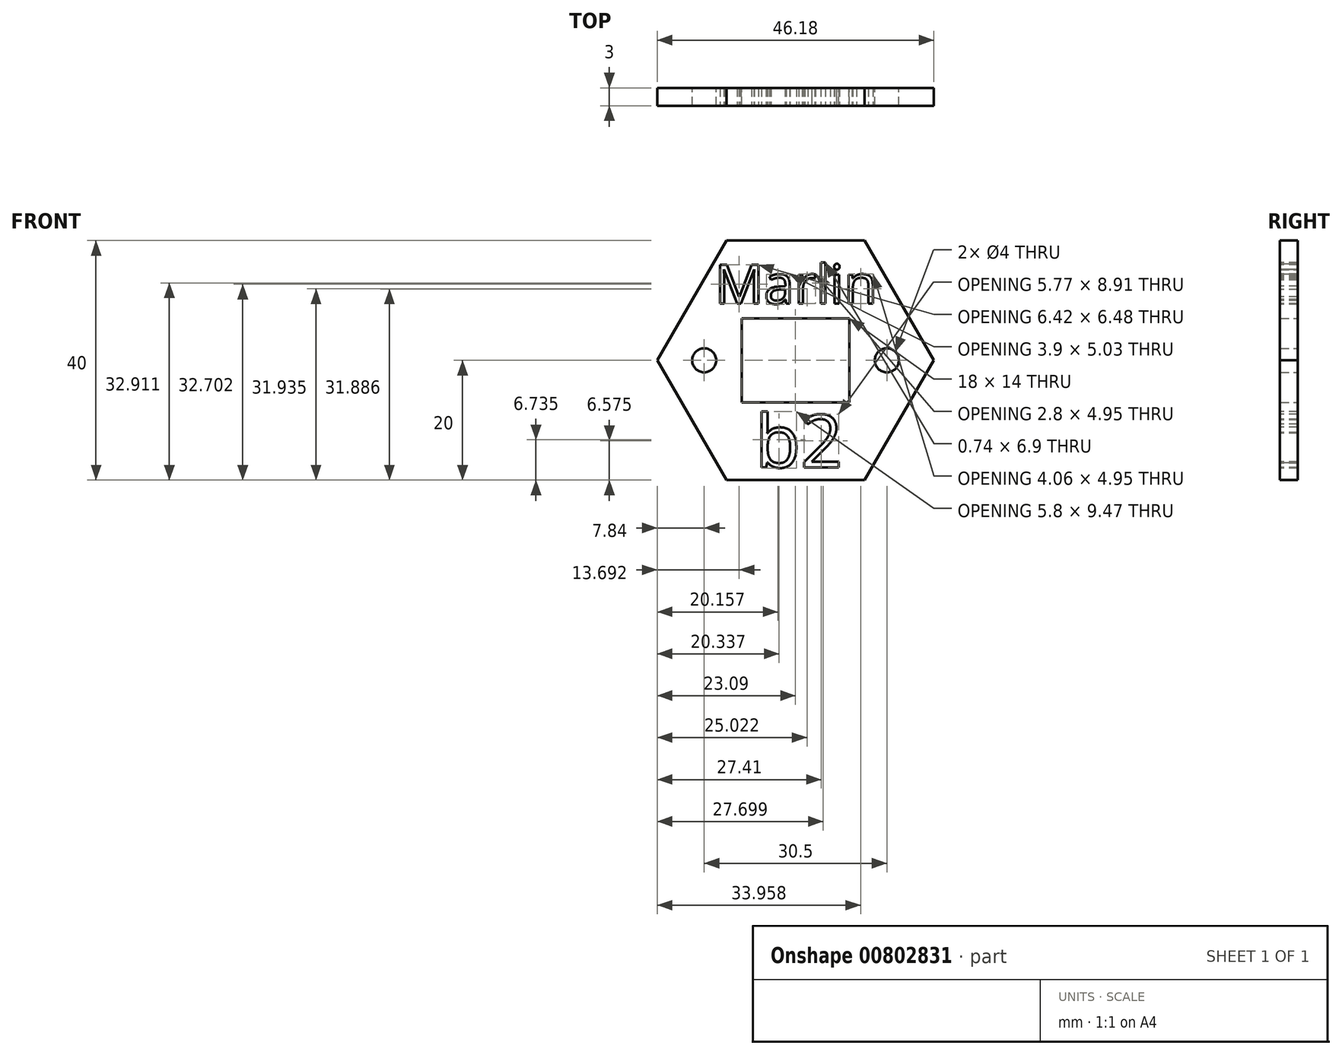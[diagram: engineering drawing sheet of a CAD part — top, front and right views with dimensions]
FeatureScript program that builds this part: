
annotation { "Feature Type Name" : "Feature", "Feature Type Description" : "" }
export const myFeature = defineFeature(function(context is Context, id is Id, definition is map)
    precondition{}
    {
        {
            var Q0;
            Q0=qCreatedBy(makeId("Front.planeOp"),FACE);
            var sketch = newSketch(context, id + "F0", { "sketchPlane" : qUnion([Q0])});
            skCircle(sketch, "E0.cCircle", {"center": v(0, 0) * mm, "radius": 20 * mm, "construction": true});
            skLineSegment(sketch, "E0.0", {"start": v(11.55, -20) * mm, "end": v(-11.55, -20) * mm});
            skLineSegment(sketch, "E0.1", {"start": v(-11.55, -20) * mm, "end": v(-23.1, 0) * mm});
            skLineSegment(sketch, "E0.2", {"start": v(-23.1, 0) * mm, "end": v(-11.55, 20) * mm});
            skLineSegment(sketch, "E0.3", {"start": v(-11.55, 20) * mm, "end": v(11.55, 20) * mm});
            skLineSegment(sketch, "E0.4", {"start": v(11.55, 20) * mm, "end": v(23.1, 0) * mm});
            skLineSegment(sketch, "E0.5", {"start": v(23.1, 0) * mm, "end": v(11.55, -20) * mm});
            skPoint(sketch, "E0.0.midPoint", {"position": v(0, -20) * mm});
            skPoint(sketch, "E1", {"position": v(15.25, 0) * mm});
            skPoint(sketch, "E2", {"position": v(-15.25, 0) * mm});
            skLineSegment(sketch, "E3.bottom", {"start": v(9, -7) * mm, "end": v(-9, -7) * mm});
            skLineSegment(sketch, "E3.top", {"start": v(9, 7) * mm, "end": v(-9, 7) * mm});
            skLineSegment(sketch, "E3.left", {"start": v(9, -7) * mm, "end": v(9, 7) * mm});
            skLineSegment(sketch, "E3.right", {"start": v(-9, -7) * mm, "end": v(-9, 7) * mm});
            skCircle(sketch, "E4", {"center": v(-15.25, 0) * mm, "radius": 2 * mm});
            skCircle(sketch, "E5", {"center": v(15.25, 0) * mm, "radius": 2 * mm});
            skSolve(sketch);
        }
        {
            var Q0;
            Q0=makeQuery(id+"F0.imprint","IMPRINT",FACE,{"disambiguationData":[TD([[makeQuery(id+"F0.imprint","IMPRINT",EDGE,{"derivedFrom":sQuery(id+"F0.wireOp",EDGE,"E0.0")}),-1.0]])]});
            extrude(context, id + "F1", {"entities" : qUnion([Q0]), "depth" : 3 * mm, "offsetDistance" : 25 * mm});
        }
        {
            var Q0;
            Q0=makeQuery(id+"F1.opExtrude","CAP_FACE",FACE,{"disambiguationData":[OSD([sQuery(id+"F0.wireOp",EDGE,"E0.0"),sQuery(id+"F0.wireOp",EDGE,"E0.1"),sQuery(id+"F0.wireOp",EDGE,"E0.2"),sQuery(id+"F0.wireOp",EDGE,"E0.3"),sQuery(id+"F0.wireOp",EDGE,"E0.4"),sQuery(id+"F0.wireOp",EDGE,"E0.5"),sQuery(id+"F0.wireOp",EDGE,"E3.bottom"),sQuery(id+"F0.wireOp",EDGE,"E3.top"),sQuery(id+"F0.wireOp",EDGE,"E3.left"),sQuery(id+"F0.wireOp",EDGE,"E3.right"),sQuery(id+"F0.wireOp",EDGE,"E4"),sQuery(id+"F0.wireOp",EDGE,"E5")])],"isStart":false});
            var sketch = newSketch(context, id + "F2", { "sketchPlane" : qUnion([Q0])});
            skText(sketch, "E6", { "text": "Marlin", "fontName": "OpenSans-Regular.ttf"});
            const initialGuessF2  = {"E6": [-0.0135, 0.00946, 1, 0, 0.00654]};
            skSetInitialGuess(sketch, initialGuessF2);
            skSolve(sketch);
        }
        {
            var Q0;
            Q0 = qSketchRegion(id + "F2", true);
            extrude(context, id + "F3", {"entities" : qUnion([Q0]), "operationType" : NewBodyOperationType.REMOVE, "oppositeDirection" : true, "depth" : 25 * mm, "offsetDistance" : 25 * mm});
        }
        {
            var Q0;
            {var subQ0=sQuery(id+"F0.wireOp",EDGE,"E3.left");var subQ1=sQuery(id+"F0.wireOp",EDGE,"E3.top");var subQ2=sQuery(id+"F0.wireOp",EDGE,"E3.bottom");var subQ3=sQuery(id+"F0.wireOp",EDGE,"E0.5");var subQ4=sQuery(id+"F0.wireOp",EDGE,"E0.4");var subQ5=sQuery(id+"F0.wireOp",EDGE,"E3.right");var subQ6=sQuery(id+"F0.wireOp",EDGE,"E0.0");var subQ7=sQuery(id+"F0.wireOp",EDGE,"E0.3");var subQ8=sQuery(id+"F0.wireOp",EDGE,"E0.1");var subQ9=sQuery(id+"F0.wireOp",EDGE,"E0.2");var subQ10=sQuery(id+"F0.wireOp",EDGE,"E4");var subQ11=sQuery(id+"F0.wireOp",EDGE,"E5");Q0=makeQuery(id+"F3.boolean.opBoolean","SPLIT",FACE,{"disambiguationData":[TD([makeQuery(id+"F1.opExtrude","SWEPT_FACE",FACE,{"disambiguationData":[OSD([subQ6])]})])],"derivedFrom":makeQuery(id+"F1.opExtrude","CAP_FACE",FACE,{"disambiguationData":[OSD([subQ6,subQ8,subQ9,subQ7,subQ4,subQ3,subQ2,subQ1,subQ0,subQ5,subQ10,subQ11])],"isStart":false})});}
            var sketch = newSketch(context, id + "F4", { "sketchPlane" : qUnion([Q0])});
            skText(sketch, "E7", { "text": "b2", "fontName": "OpenSans-Regular.ttf"});
            const initialGuessF4  = {"E7": [-0.00671, -0.01788, 1, 0, 0.00886]};
            skSetInitialGuess(sketch, initialGuessF4);
            skSolve(sketch);
        }
        {
            var Q0;
            Q0=makeQuery(id+"F4.imprint","IMPRINT",FACE,{"disambiguationData":[TD([[makeQuery(id+"F4.imprint","IMPRINT",EDGE,{"derivedFrom":sQuery(id+"F4.wireOp",EDGE,"E7.sketch_text.stroke-0")}),-1.0]])]});
            var Q1;
            Q1=makeQuery(id+"F4.imprint","IMPRINT",FACE,{"disambiguationData":[TD([[makeQuery(id+"F4.imprint","IMPRINT",EDGE,{"derivedFrom":sQuery(id+"F4.wireOp",EDGE,"E7.sketch_text.stroke-23")}),-1.0]])]});
            extrude(context, id + "F5", {"entities" : qUnion([Q0, Q1]), "operationType" : NewBodyOperationType.REMOVE, "oppositeDirection" : true, "depth" : 25 * mm, "offsetDistance" : 25 * mm});
        }
    });
